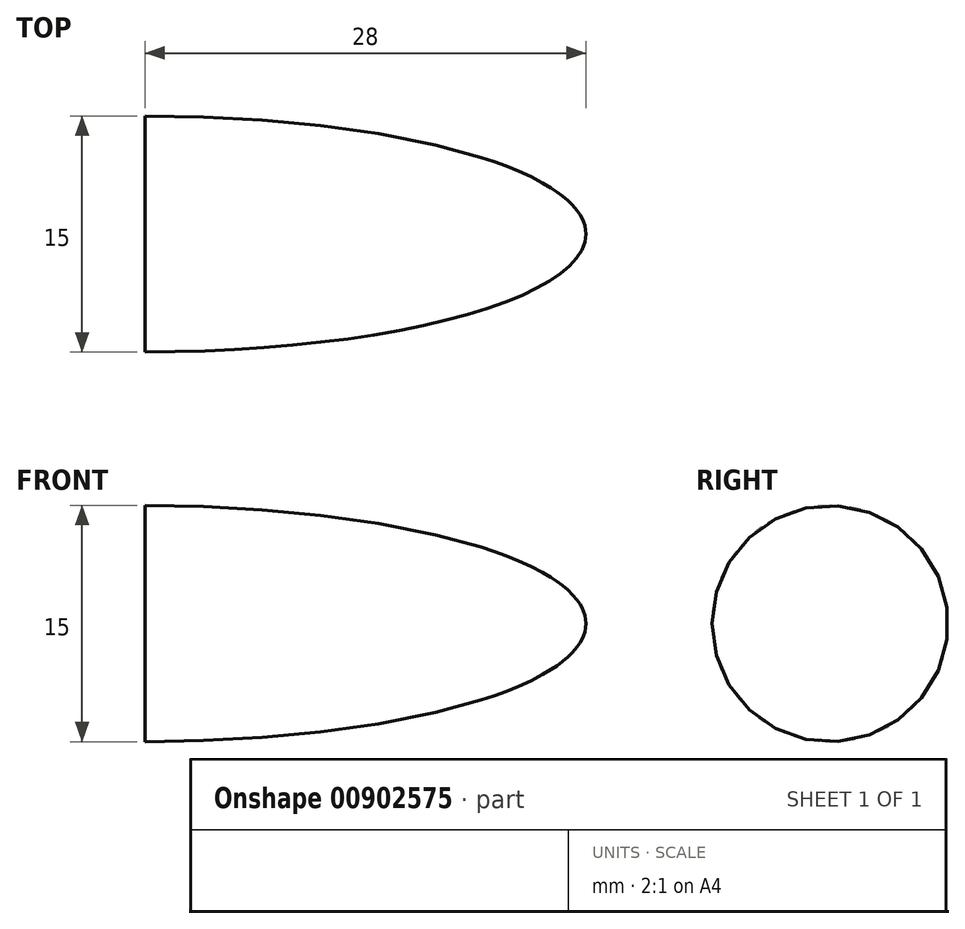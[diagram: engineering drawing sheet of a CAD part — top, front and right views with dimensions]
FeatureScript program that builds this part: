
annotation { "Feature Type Name" : "Feature", "Feature Type Description" : "" }
export const myFeature = defineFeature(function(context is Context, id is Id, definition is map)
    precondition{}
    {
        {
            var Q0;
            Q0=qCreatedBy(makeId("Top.planeOp"),FACE);
            var sketch = newSketch(context, id + "F0", { "sketchPlane" : qUnion([Q0])});
            skEllipse(sketch, "E0", {"center": v(0, 0) * mm, "majorRadius": 28 * mm, "minorRadius": 7.5 * mm, "majorAxis": v(1, 0)});
            skLineSegment(sketch, "E1", {"start": v(-73.74, 0) * mm, "end": v(68.92, 0) * mm});
            skLineSegment(sketch, "E2.bottom", {"start": v(0, 40.75) * mm, "end": v(44.77, 40.75) * mm});
            skLineSegment(sketch, "E2.top", {"start": v(0, -54.24) * mm, "end": v(44.77, -54.24) * mm});
            skLineSegment(sketch, "E2.left", {"start": v(0, 40.75) * mm, "end": v(0, -54.24) * mm});
            skLineSegment(sketch, "E2.right", {"start": v(44.77, 40.75) * mm, "end": v(44.77, -54.24) * mm});
            skLineSegment(sketch, "E3.bottom", {"start": v(-45.02, 0) * mm, "end": v(65.73, 0) * mm});
            skLineSegment(sketch, "E3.top", {"start": v(-45.02, -42) * mm, "end": v(65.73, -42) * mm});
            skLineSegment(sketch, "E3.left", {"start": v(-45.02, 0) * mm, "end": v(-45.02, -42) * mm});
            skLineSegment(sketch, "E3.right", {"start": v(65.73, 0) * mm, "end": v(65.73, -42) * mm});
            skSolve(sketch);
        }
        {
            var Q0;
            {var subQ0=sQuery(id+"F0.wireOp",EDGE,"E2.left");var subQ1=sQuery(id+"F0.wireOp",EDGE,"E0");var subQ2=makeQuery(id+"F0.imprint","INTERSECT",VERTEX,{"disambiguationData":[OD(0.0)],"derivedFrom":[subQ1,subQ0]});Q0=makeQuery(id+"F0.imprint","IMPRINT",FACE,{"disambiguationData":[TD([[makeQuery(id+"F0.imprint","IMPRINT",EDGE,{"disambiguationData":[TD([[subQ2,-1.0]])],"derivedFrom":subQ1}),1.0]])]});}
            var Q1;
            Q1=sQuery(id+"F0.wireOp",EDGE,"E1");
            revolve(context, id + "F1", {"surfaceOperationType" : NewSurfaceOperationType.NEW, "entities" : qUnion([Q0]), "axis" : qUnion([Q1]), "revolveType" : RevolveType.FULL});
        }
    });
